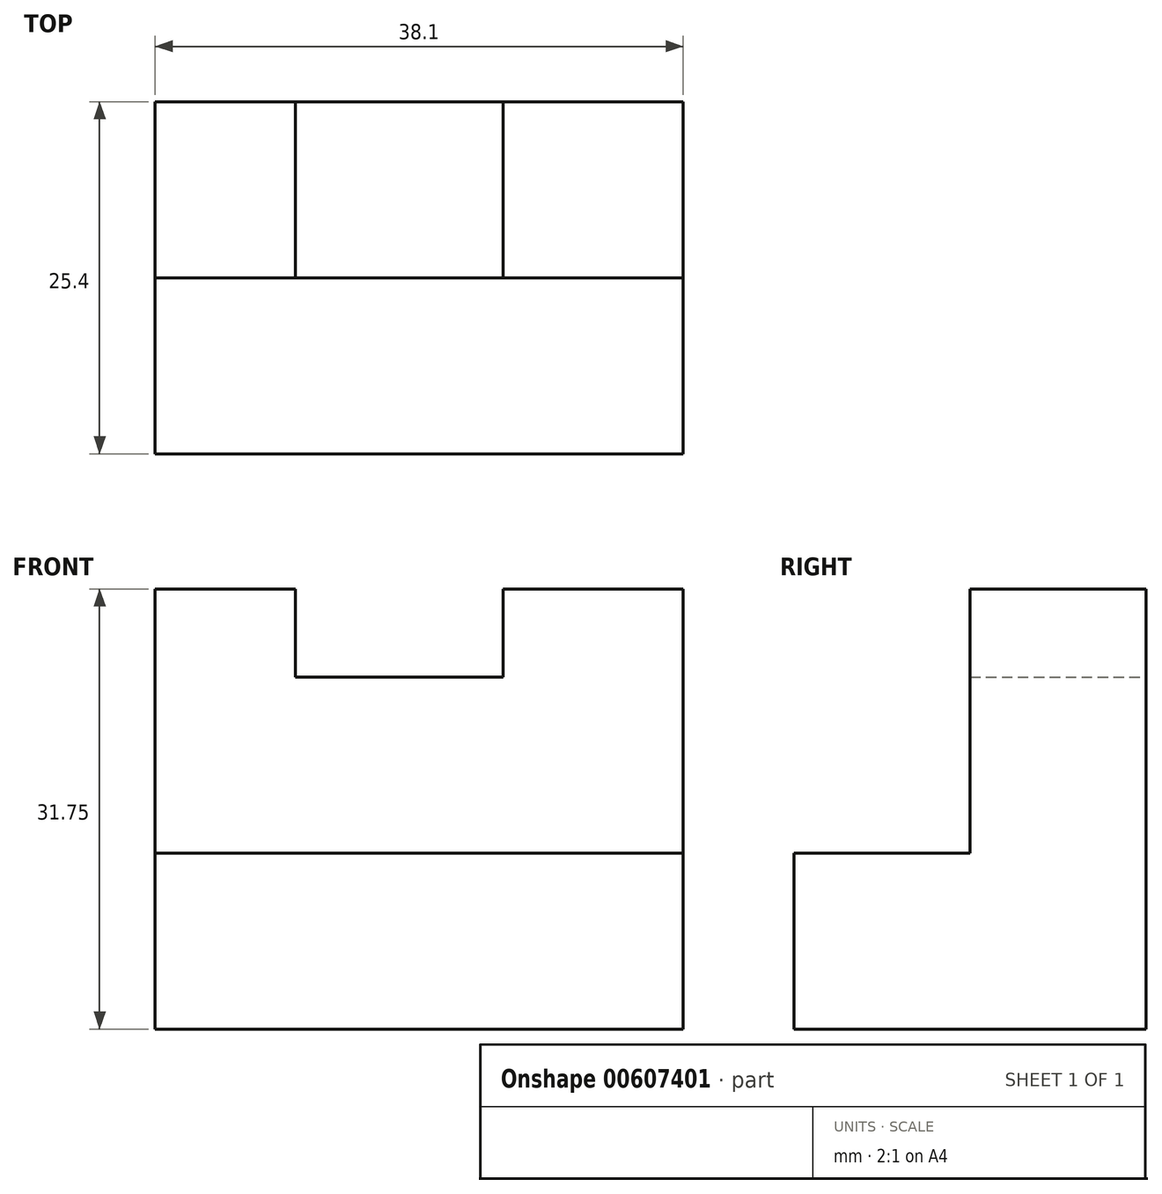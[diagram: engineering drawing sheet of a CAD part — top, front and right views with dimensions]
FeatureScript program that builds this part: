
annotation { "Feature Type Name" : "Feature", "Feature Type Description" : "" }
export const myFeature = defineFeature(function(context is Context, id is Id, definition is map)
    precondition{}
    {
        {
            var Q0;
            Q0=qCreatedBy(makeId("Right.planeOp"),FACE);
            var sketch = newSketch(context, id + "F0", { "sketchPlane" : qUnion([Q0])});
            skLineSegment(sketch, "E0", {"start": v(0, 0) * mm, "end": v(0, 31.75) * mm});
            skLineSegment(sketch, "E1", {"start": v(0, 31.75) * mm, "end": v(-12.7, 31.75) * mm});
            skLineSegment(sketch, "E2", {"start": v(-12.7, 31.75) * mm, "end": v(-12.7, 12.7) * mm});
            skLineSegment(sketch, "E3", {"start": v(-12.7, 12.7) * mm, "end": v(-25.4, 12.7) * mm});
            skLineSegment(sketch, "E4", {"start": v(-25.4, 12.7) * mm, "end": v(-25.4, 0) * mm});
            skLineSegment(sketch, "E5", {"start": v(-25.4, 0) * mm, "end": v(0, 0) * mm});
            skSolve(sketch);
        }
        {
            var Q0;
            Q0 = qSketchRegion(id + "F0", true);
            extrude(context, id + "F1", {"entities" : qUnion([Q0]), "depth" : 25.4 * mm, "offsetDistance" : 25.4 * mm});
        }
        {
            var Q0;
            Q0=makeQuery(id+"F1.opExtrude","CAP_FACE",FACE,{"disambiguationData":[OSD([sQuery(id+"F0.wireOp",EDGE,"E0"),sQuery(id+"F0.wireOp",EDGE,"E1"),sQuery(id+"F0.wireOp",EDGE,"E2"),sQuery(id+"F0.wireOp",EDGE,"E3"),sQuery(id+"F0.wireOp",EDGE,"E4"),sQuery(id+"F0.wireOp",EDGE,"E5")])],"isStart":false});
            extrude(context, id + "F2", {"entities" : qUnion([Q0]), "operationType" : NewBodyOperationType.ADD, "depth" : 12.7 * mm, "offsetDistance" : 25.4 * mm});
        }
        {
            var Q0;
            {var subQ0=sQuery(id+"F0.wireOp",EDGE,"E1");Q0=makeQuery(id+"F2.boolean.opBoolean","MERGE",FACE,{"derivedFrom":[makeQuery(id+"F1.opExtrude","SWEPT_FACE",FACE,{"disambiguationData":[OSD([subQ0])]}),makeQuery(id+"F2.opExtrude","SWEPT_FACE",FACE,{"disambiguationData":[OSD([subQ0])]})]});}
            var sketch = newSketch(context, id + "F3", { "sketchPlane" : qUnion([Q0])});
            skLineSegment(sketch, "E6", {"start": v(10.13, -12.7) * mm, "end": v(10.13, 0) * mm});
            skLineSegment(sketch, "E7", {"start": v(25.11, -12.7) * mm, "end": v(25.11, 0) * mm});
            skSolve(sketch);
        }
        {
            var Q0;
            {var subQ0=sQuery(id+"F3.wireOp",EDGE,"E6");Q0=makeQuery(id+"F3.imprint","IMPRINT",FACE,{"disambiguationData":[TD([[makeQuery(id+"F3.imprint","IMPRINT",EDGE,{"derivedFrom":subQ0}),-1.0]])]});}
            extrude(context, id + "F4", {"entities" : qUnion([Q0]), "operationType" : NewBodyOperationType.REMOVE, "oppositeDirection" : true, "depth" : 6.35 * mm, "offsetDistance" : 25.4 * mm});
        }
    });
